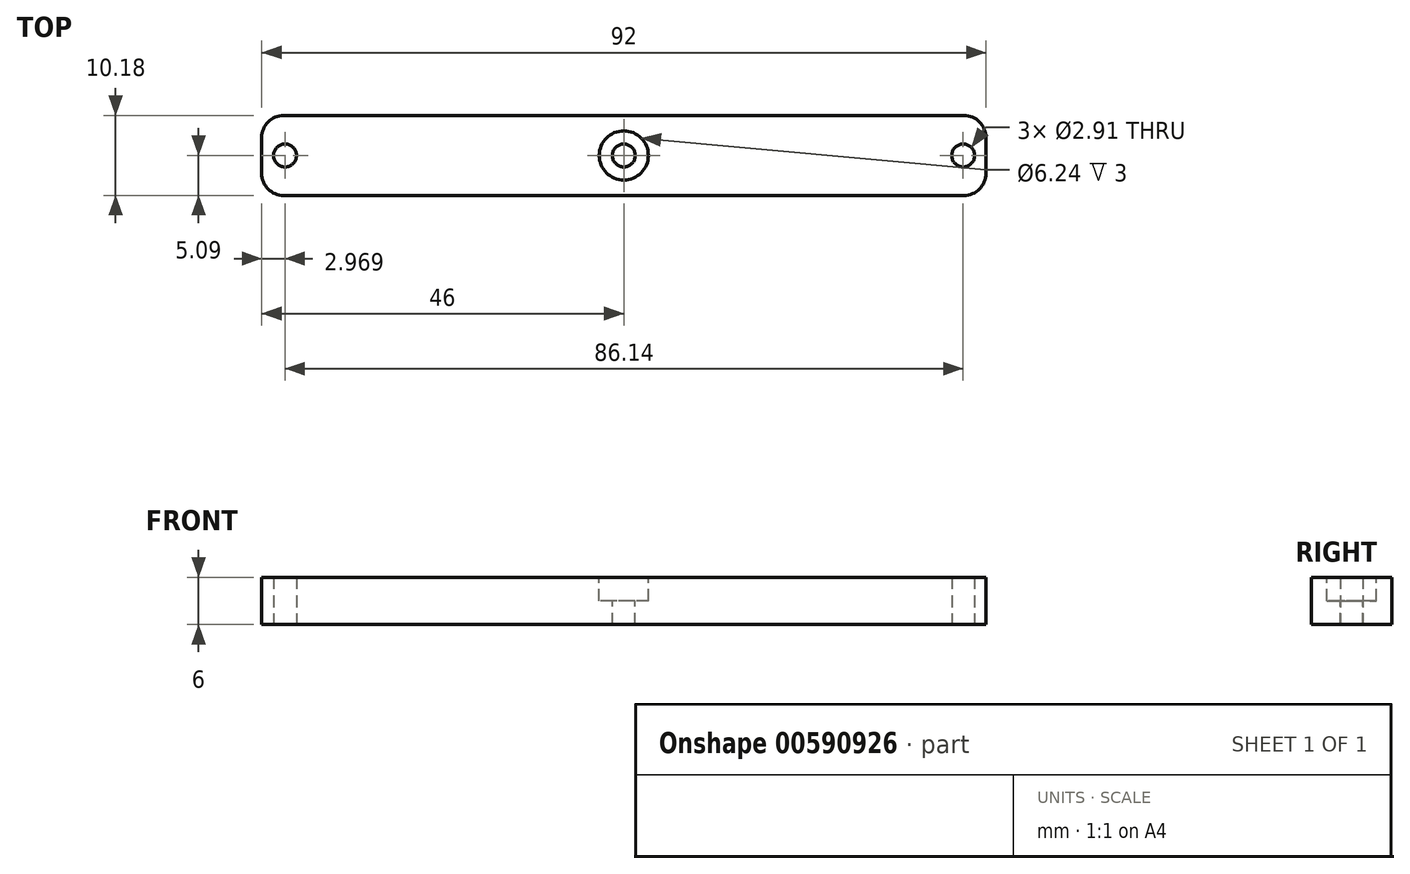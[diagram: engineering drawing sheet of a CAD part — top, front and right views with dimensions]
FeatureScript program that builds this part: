
annotation { "Feature Type Name" : "Feature", "Feature Type Description" : "" }
export const myFeature = defineFeature(function(context is Context, id is Id, definition is map)
    precondition{}
    {
        {
            var Q0;
            Q0=qCreatedBy(makeId("Top.planeOp"),FACE);
            var sketch = newSketch(context, id + "F0", { "sketchPlane" : qUnion([Q0])});
            skLineSegment(sketch, "E0.bottom", {"start": v(46, 5.09) * mm, "end": v(-46, 5.09) * mm});
            skLineSegment(sketch, "E0.top", {"start": v(46, -5.09) * mm, "end": v(-46, -5.09) * mm});
            skLineSegment(sketch, "E0.left", {"start": v(46, 5.09) * mm, "end": v(46, -5.09) * mm});
            skLineSegment(sketch, "E0.right", {"start": v(-46, 5.09) * mm, "end": v(-46, -5.09) * mm});
            skPoint(sketch, "E0.middle", {"position": v(0, 0) * mm});
            skCircle(sketch, "E1", {"center": v(-43.03, 0) * mm, "radius": 1.46 * mm});
            skCircle(sketch, "E2", {"center": v(43.1, 0) * mm, "radius": 1.45 * mm});
            skSolve(sketch);
        }
        {
            var Q0;
            Q0=makeQuery(id+"F0.imprint","IMPRINT",FACE,{"disambiguationData":[TD([[makeQuery(id+"F0.imprint","IMPRINT",EDGE,{"derivedFrom":sQuery(id+"F0.wireOp",EDGE,"E0.bottom")}),1.0]])]});
            extrude(context, id + "F1", {"entities" : qUnion([Q0]), "endBound" : BoundingType.SYMMETRIC, "depth" : 6 * mm, "offsetDistance" : 25.4 * mm});
        }
        {
            var Q0;
            Q0=makeQuery(id+"F1.opExtrude","SWEPT_EDGE",EDGE,{"disambiguationData":[OSD([sQuery(id+"F0.wireOp",EDGE,"E0.bottom"),sQuery(id+"F0.wireOp",EDGE,"E0.right")])]});
            var Q1;
            Q1=makeQuery(id+"F1.opExtrude","SWEPT_EDGE",EDGE,{"disambiguationData":[OSD([sQuery(id+"F0.wireOp",EDGE,"E0.top"),sQuery(id+"F0.wireOp",EDGE,"E0.right")])]});
            var Q2;
            Q2=makeQuery(id+"F1.opExtrude","SWEPT_EDGE",EDGE,{"disambiguationData":[OSD([sQuery(id+"F0.wireOp",EDGE,"E0.bottom"),sQuery(id+"F0.wireOp",EDGE,"E0.left")])]});
            var Q3;
            Q3=makeQuery(id+"F1.opExtrude","SWEPT_EDGE",EDGE,{"disambiguationData":[OSD([sQuery(id+"F0.wireOp",EDGE,"E0.top"),sQuery(id+"F0.wireOp",EDGE,"E0.left")])]});
            fillet(context, id + "F2", {"entities" : qUnion([Q0, Q1, Q2, Q3]), "radius" : 2.8 * mm, "tangentPropagation" : true, "allowEdgeOverflow" : false});
        }
        {
            var Q0;
            Q0=makeQuery(id+"F1.opExtrude","CAP_FACE",FACE,{"disambiguationData":[OSD([sQuery(id+"F0.wireOp",EDGE,"E0.bottom"),sQuery(id+"F0.wireOp",EDGE,"E0.top"),sQuery(id+"F0.wireOp",EDGE,"E0.left"),sQuery(id+"F0.wireOp",EDGE,"E0.right"),sQuery(id+"F0.wireOp",EDGE,"E1"),sQuery(id+"F0.wireOp",EDGE,"E2")])],"isStart":false});
            var sketch = newSketch(context, id + "F3", { "sketchPlane" : qUnion([Q0])});
            skCircle(sketch, "E3", {"center": v(0, 0) * mm, "radius": 3.12 * mm});
            skSolve(sketch);
        }
        {
            var Q0;
            Q0 = qSketchRegion(id + "F3", true);
            extrude(context, id + "F4", {"entities" : qUnion([Q0]), "operationType" : NewBodyOperationType.REMOVE, "endBound" : BoundingType.SYMMETRIC, "oppositeDirection" : true, "depth" : 6 * mm, "offsetDistance" : 25.4 * mm});
        }
        {
            var Q0;
            Q0=qCreatedBy(makeId("Top.planeOp"),FACE);
            var sketch = newSketch(context, id + "F5", { "sketchPlane" : qUnion([Q0])});
            skCircle(sketch, "E4", {"center": v(0, 0) * mm, "radius": 1.45 * mm});
            skSolve(sketch);
        }
        {
            var Q0;
            Q0 = qSketchRegion(id + "F5", true);
            extrude(context, id + "F6", {"entities" : qUnion([Q0]), "operationType" : NewBodyOperationType.REMOVE, "endBound" : BoundingType.SYMMETRIC, "oppositeDirection" : true, "depth" : 6 * mm, "offsetDistance" : 25.4 * mm});
        }
    });
